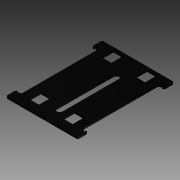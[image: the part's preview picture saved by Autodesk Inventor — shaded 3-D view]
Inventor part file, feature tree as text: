
AUTODESK INVENTOR PART (.ipt)
format: ipt  version: 2013 (Build 170138000, 138)  size: 249,856 bytes
history: native  units: mm
features: extrude x9, sketch x9, mirror x3, reference x3, fillet x1
ambient origin geometry x8: Origin, YZ Plane, XZ Plane, XY Plane, X Axis, Y Axis, Z Axis, Center Point
bodies: Solid1 (feature_tree)
feature tree (25):
  extrude  "Extrusion1"  Depth=254.0mm
  extrude  "Extrusion2"  Depth=270.0mm
  extrude  "Extrusion3"  Depth=6.477mm TaperAngle=0.0deg
  extrude  "Extrusion4"  TaperAngle=135.0deg  [1 undecoded]
  fillet  "Fillet1"  Radius=8.0mm
  mirror  "Mirror1"
  mirror  "Mirror2"
  mirror  "Mirror3"
  extrude  "Extrusion5"  Depth=4.0mm
  extrude  "Extrusion6"  Depth=1.0mm
  extrude  "Extrusion7"  Depth=5.0mm
  extrude  "Extrusion8"  Depth=6.477mm TaperAngle=0.0deg
  extrude  "Extrusion9"  Depth=11.0mm
  sketch  "Sketch1"  dims[d0=340.0mm d2=254.0mm]
  sketch  "Sketch2"  dims[d3=6.477mm d4=0.0mm d5=270.0mm]
  sketch  "Sketch3"  dims[d7=20.0mm d8=6.477mm d9=0.0mm]
  sketch  "Sketch4"  dims[d10=10.0mm d12=135.0deg d14=8.0mm]
  sketch  "Sketch5"  dims[d15=6.477mm d16=0.0mm d17=4.0mm]
  sketch  "Sketch6"  dims[d19=8.0mm d20=1.0mm]
  reference  "Reference1"
  sketch  "Sketch7"  dims[d21=6.477mm d22=0.0mm d23=5.0mm]
  sketch  "Sketch8"  dims[d24=2.5mm d28=6.477mm d29=0.0mm]
  reference  "Reference2"
  sketch  "Sketch9"  dims[d31=18.5mm d32=11.0mm d33=200.0mm d34=9.5mm d35=20.0mm d36=10.0mm d37=0.0mm d38=2.5mm d40=5.0mm d41=10.0mm d42=0.0mm d43=10.0mm d44=0.0mm d45=10.0mm d46=0.0mm]
  reference  "Reference3"
note: 1 required parameter value undecoded (feature->parameter linkage not recoverable at this tier; creation-order binding heuristic only, values carry confidence <= 0.55)
